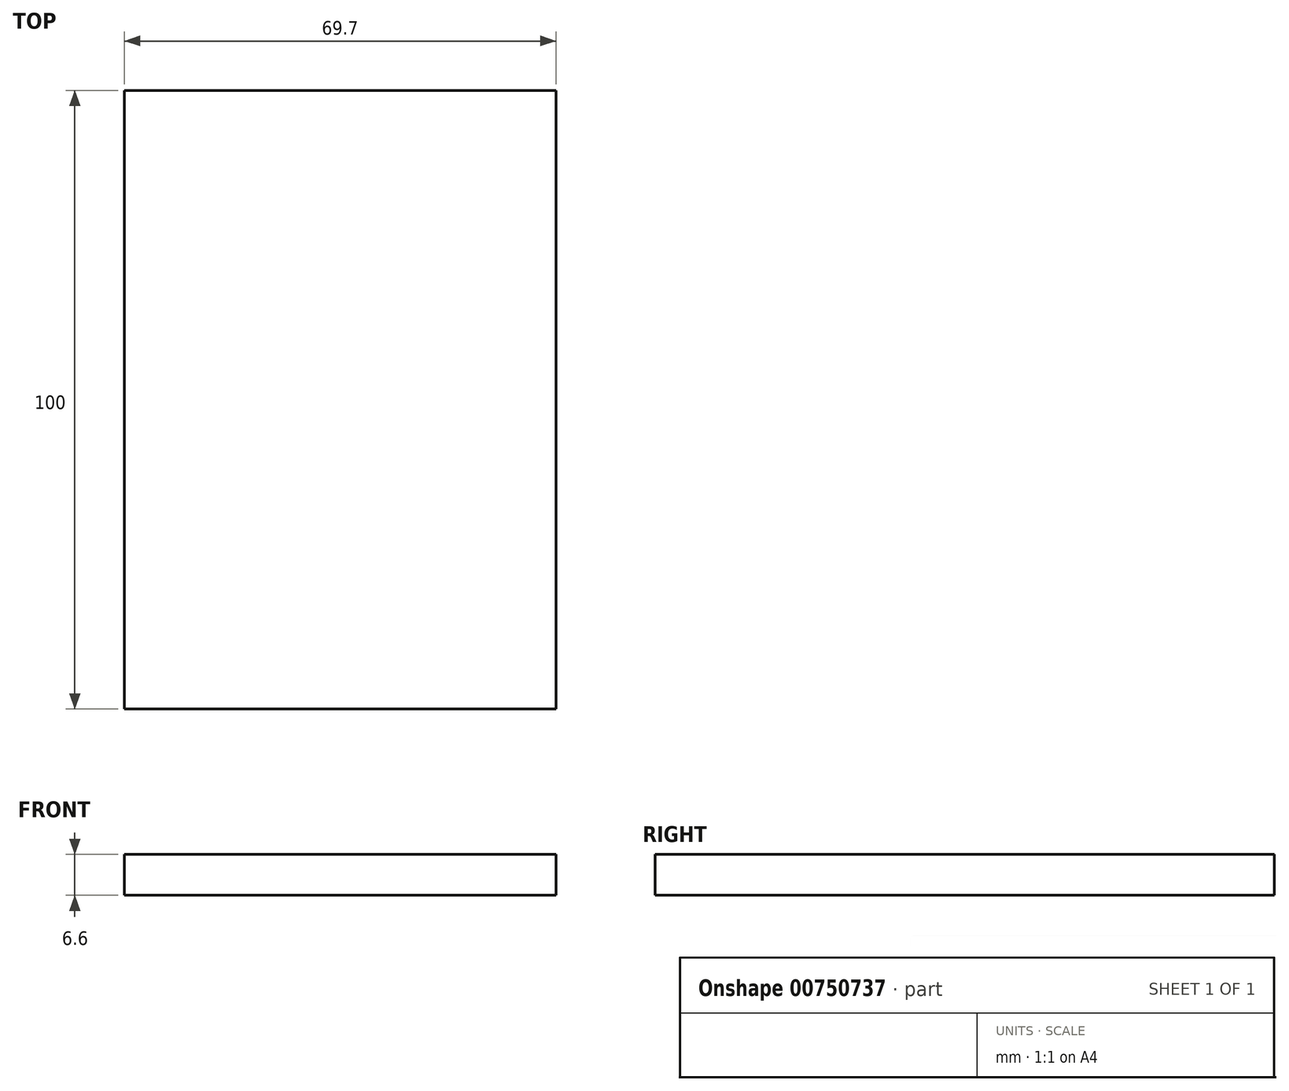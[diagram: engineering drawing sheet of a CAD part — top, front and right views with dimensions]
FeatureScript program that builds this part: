
annotation { "Feature Type Name" : "Feature", "Feature Type Description" : "" }
export const myFeature = defineFeature(function(context is Context, id is Id, definition is map)
    precondition{}
    {
        {
            var Q0;
            Q0=qCreatedBy(makeId("Top.planeOp"),FACE);
            var sketch = newSketch(context, id + "F0", { "sketchPlane" : qUnion([Q0])});
            skLineSegment(sketch, "E0.bottom", {"start": v(34.85, -50) * mm, "end": v(-34.85, -50) * mm});
            skLineSegment(sketch, "E0.top", {"start": v(34.85, 50) * mm, "end": v(-34.85, 50) * mm});
            skLineSegment(sketch, "E0.left", {"start": v(34.85, -50) * mm, "end": v(34.85, 50) * mm});
            skLineSegment(sketch, "E0.right", {"start": v(-34.85, -50) * mm, "end": v(-34.85, 50) * mm});
            skPoint(sketch, "E0.middle", {"position": v(0, 0) * mm});
            skSolve(sketch);
        }
        {
            var Q0;
            Q0 = qSketchRegion(id + "F0", true);
            extrude(context, id + "F1", {"entities" : qUnion([Q0]), "depth" : 6.6 * mm, "offsetDistance" : 25 * mm});
        }
    });
